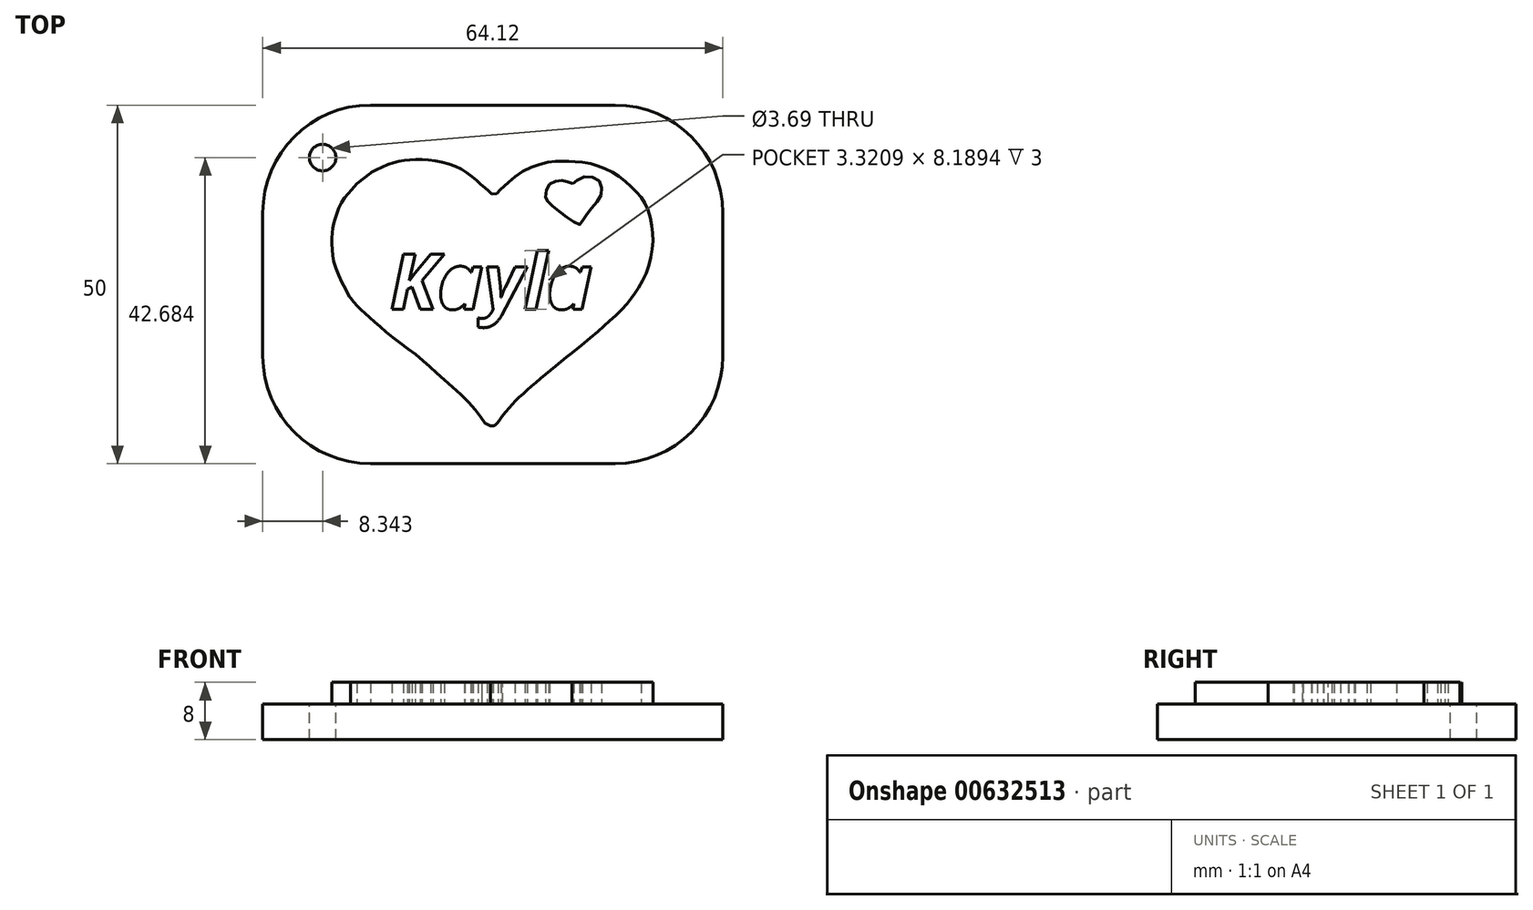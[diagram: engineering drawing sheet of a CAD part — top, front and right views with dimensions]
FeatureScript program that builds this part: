
annotation { "Feature Type Name" : "Feature", "Feature Type Description" : "" }
export const myFeature = defineFeature(function(context is Context, id is Id, definition is map)
    precondition{}
    {
        {
            var Q0;
            Q0=qCreatedBy(makeId("Top.planeOp"),FACE);
            var sketch = newSketch(context, id + "F0", { "sketchPlane" : qUnion([Q0])});
            skFitSpline(sketch, "E0", {"points": [v(-10.22, 16.07) * mm, v(-11.83, 17.48) * mm, v(-14.68, 19.6) * mm, v(-18.7, 20.74) * mm, v(-22.17, 20.77) * mm, v(-24.92, 20.07) * mm, v(-27.15, 18.98) * mm, v(-27.15, 18.96) * mm], "startDerivative": vector(-10.74, 9.94) * mm, "endDerivative": vector(0.77, -1.4) * mm});
            skFitSpline(sketch, "E1", {"points": [v(-29.04, 17.5) * mm, v(-27.15, 18.96) * mm], "startDerivative": vector(1.9, 1.45) * mm, "endDerivative": vector(1.9, 1.45) * mm});
            skFitSpline(sketch, "E2", {"points": [v(-29.04, 17.5) * mm, v(-29.87, 16.55) * mm, v(-31.22, 14.8) * mm, v(-32.12, 12.42) * mm, v(-32.46, 10.95) * mm, v(-32.51, 8.74) * mm, v(-32.07, 5.97) * mm, v(-30.44, 2.44) * mm, v(-29.97, 1.59) * mm, v(-29.92, 1.55) * mm], "startDerivative": vector(-7.96, -9.41) * mm, "endDerivative": vector(1.7, 0.61) * mm});
            skPoint(sketch, "E3.4.internal.orphan", {"position": v(-28.84, 0) * mm});
            skFitSpline(sketch, "E4", {"points": [v(-29.92, 1.55) * mm, v(-29.34, 0.8) * mm, v(-28.54, 0) * mm, v(-27.77, -0.74) * mm, v(-26.51, -1.83) * mm, v(-24.83, -3.28) * mm, v(-22.4, -5.19) * mm, v(-19.63, -7.33) * mm, v(-17.14, -9.63) * mm, v(-13.78, -12.64) * mm, v(-11.6, -15.33) * mm, v(-10.45, -16.28) * mm], "startDerivative": vector(9.33, -13.02) * mm, "endDerivative": vector(23.6, -0.7) * mm});
            skFitSpline(sketch, "E5", {"points": [v(-10.45, -16.28) * mm, v(-10.15, -16.28) * mm, v(-9.62, -16.03) * mm, v(-8.8, -14.99) * mm, v(-6.9, -12.79) * mm, v(-3.84, -10) * mm, v(0.92, -6.08) * mm], "startDerivative": vector(4.47, -0.42) * mm, "endDerivative": vector(17.48, 14.25) * mm});
            skFitSpline(sketch, "E6", {"points": [v(0.92, -6.08) * mm, v(4.47, -3.2) * mm, v(6.2, -1.62) * mm, v(7.96, 0) * mm, v(9.24, 1.54) * mm, v(10.05, 2.7) * mm, v(11.15, 4.8) * mm, v(11.9, 7.15) * mm, v(12.23, 9.6) * mm, v(12.05, 11.74) * mm, v(11.45, 13.98) * mm, v(10.59, 15.59) * mm], "startDerivative": vector(30.84, 24.32) * mm, "endDerivative": vector(-11.6, 18.83) * mm});
            skFitSpline(sketch, "E7", {"points": [v(10.59, 15.59) * mm, v(9.74, 16.54) * mm, v(8.74, 17.45) * mm, v(7.63, 18.4) * mm, v(6.4, 19.22) * mm, v(4.86, 19.85) * mm, v(3.79, 20.23) * mm, v(2.19, 20.5) * mm, v(1.1, 20.6) * mm, v(0, 20.6) * mm, v(-0.98, 20.6) * mm, v(-2.16, 20.53) * mm, v(-3.8, 20.13) * mm, v(-5.62, 19.4) * mm, v(-7.32, 18.23) * mm, v(-8.3, 17.37) * mm, v(-8.75, 16.96) * mm, v(-9.2, 16.5) * mm, v(-9.66, 16.08) * mm, v(-10.22, 16.07) * mm], "startDerivative": vector(-15.27, 18.1) * mm, "endDerivative": vector(-17.36, -0.4) * mm});
            skLineSegment(sketch, "E8", {"start": v(0.92, 17.65) * mm, "end": v(1.03, 17.5) * mm});
            skPoint(sketch, "E9.5.internal.orphan", {"position": v(0.72, 17.74) * mm});
            skPoint(sketch, "E10.6.internal.orphan", {"position": v(0, 13.29) * mm});
            skPoint(sketch, "E10.start.orphan", {"position": v(-1.58, 17.74) * mm});
            skPoint(sketch, "E11.1.internal.orphan", {"position": v(1.18, 17.5) * mm});
            skPoint(sketch, "E11.10.internal.orphan", {"position": v(5.07, 17.5) * mm});
            skFitSpline(sketch, "E12", {"points": [v(-1.92, 17.58) * mm, v(-2.49, 17.03) * mm, v(-2.78, 15.75) * mm, v(-2.68, 15.38) * mm, v(-2.28, 14.8) * mm, v(-1.48, 14.1) * mm, v(0.14, 12.9) * mm, v(1.34, 12.1) * mm, v(2.06, 11.83) * mm, v(2.48, 12.48) * mm, v(3.02, 13.29) * mm, v(3.77, 14.25) * mm, v(4.74, 15.39) * mm, v(5.07, 16.5) * mm, v(4.9, 17.64) * mm, v(3.99, 18.34) * mm, v(2.58, 18.46) * mm, v(1.43, 17.77) * mm, v(1.03, 17.5) * mm, v(0.47, 17.7) * mm, v(-0.21, 17.92) * mm, v(-1.05, 17.92) * mm, v(-1.92, 17.58) * mm]});
            skText(sketch, "E13", { "text": "Kayla", "fontName": "OpenSans-BoldItalic.ttf"});
            const initialGuessF0  = {"E13": [-0.02444, 0, 1, 0, 0.00776]};
            skSetInitialGuess(sketch, initialGuessF0);
            skSolve(sketch);
        }
        {
            var Q0;
            Q0=makeQuery(id+"F0.imprint","IMPRINT",FACE,{"disambiguationData":[TD([[makeQuery(id+"F0.imprint","IMPRINT",EDGE,{"derivedFrom":sQuery(id+"F0.wireOp",EDGE,"E0")}),1.0]])]});
            var Q1;
            Q1=makeQuery(id+"F0.imprint","IMPRINT",FACE,{"disambiguationData":[TD([[makeQuery(id+"F0.imprint","IMPRINT",EDGE,{"derivedFrom":sQuery(id+"F0.wireOp",EDGE,"f24f585c-4cd1-4648-b118-72204d16ea68.sketch_text.stroke-28")}),1.0]])]});
            var Q2;
            Q2=makeQuery(id+"F0.imprint","IMPRINT",FACE,{"disambiguationData":[TD([[makeQuery(id+"F0.imprint","IMPRINT",EDGE,{"derivedFrom":sQuery(id+"F0.wireOp",EDGE,"f24f585c-4cd1-4648-b118-72204d16ea68.sketch_text.stroke-74")}),1.0]])]});
            extrude(context, id + "F1", {"entities" : qUnion([Q0, Q1, Q2]), "depth" : 3 * mm, "offsetDistance" : 25 * mm});
        }
        {
            var Q0;
            Q0=makeQuery(id+"F1.opExtrude","CAP_FACE",FACE,{"disambiguationData":[OSD([sQuery(id+"F0.wireOp",EDGE,"E0"),sQuery(id+"F0.wireOp",EDGE,"E1"),sQuery(id+"F0.wireOp",EDGE,"E2"),sQuery(id+"F0.wireOp",EDGE,"E4"),sQuery(id+"F0.wireOp",EDGE,"E5"),sQuery(id+"F0.wireOp",EDGE,"E6"),sQuery(id+"F0.wireOp",EDGE,"E7"),sQuery(id+"F0.wireOp",EDGE,"f24f585c-4cd1-4648-b118-72204d16ea68.sketch_text.stroke-0"),sQuery(id+"F0.wireOp",EDGE,"f24f585c-4cd1-4648-b118-72204d16ea68.sketch_text.stroke-1"),sQuery(id+"F0.wireOp",EDGE,"f24f585c-4cd1-4648-b118-72204d16ea68.sketch_text.stroke-2"),sQuery(id+"F0.wireOp",EDGE,"f24f585c-4cd1-4648-b118-72204d16ea68.sketch_text.stroke-3"),sQuery(id+"F0.wireOp",EDGE,"f24f585c-4cd1-4648-b118-72204d16ea68.sketch_text.stroke-4"),sQuery(id+"F0.wireOp",EDGE,"f24f585c-4cd1-4648-b118-72204d16ea68.sketch_text.stroke-5"),sQuery(id+"F0.wireOp",EDGE,"f24f585c-4cd1-4648-b118-72204d16ea68.sketch_text.stroke-6"),sQuery(id+"F0.wireOp",EDGE,"f24f585c-4cd1-4648-b118-72204d16ea68.sketch_text.stroke-7"),sQuery(id+"F0.wireOp",EDGE,"f24f585c-4cd1-4648-b118-72204d16ea68.sketch_text.stroke-8"),sQuery(id+"F0.wireOp",EDGE,"f24f585c-4cd1-4648-b118-72204d16ea68.sketch_text.stroke-9"),sQuery(id+"F0.wireOp",EDGE,"f24f585c-4cd1-4648-b118-72204d16ea68.sketch_text.stroke-10"),sQuery(id+"F0.wireOp",EDGE,"f24f585c-4cd1-4648-b118-72204d16ea68.sketch_text.stroke-11"),sQuery(id+"F0.wireOp",EDGE,"f24f585c-4cd1-4648-b118-72204d16ea68.sketch_text.stroke-12"),sQuery(id+"F0.wireOp",EDGE,"f24f585c-4cd1-4648-b118-72204d16ea68.sketch_text.stroke-13"),sQuery(id+"F0.wireOp",EDGE,"f24f585c-4cd1-4648-b118-72204d16ea68.sketch_text.stroke-14"),sQuery(id+"F0.wireOp",EDGE,"f24f585c-4cd1-4648-b118-72204d16ea68.sketch_text.stroke-15"),sQuery(id+"F0.wireOp",EDGE,"f24f585c-4cd1-4648-b118-72204d16ea68.sketch_text.stroke-16"),sQuery(id+"F0.wireOp",EDGE,"f24f585c-4cd1-4648-b118-72204d16ea68.sketch_text.stroke-17"),sQuery(id+"F0.wireOp",EDGE,"f24f585c-4cd1-4648-b118-72204d16ea68.sketch_text.stroke-18"),sQuery(id+"F0.wireOp",EDGE,"f24f585c-4cd1-4648-b118-72204d16ea68.sketch_text.stroke-19"),sQuery(id+"F0.wireOp",EDGE,"f24f585c-4cd1-4648-b118-72204d16ea68.sketch_text.stroke-20"),sQuery(id+"F0.wireOp",EDGE,"f24f585c-4cd1-4648-b118-72204d16ea68.sketch_text.stroke-21"),sQuery(id+"F0.wireOp",EDGE,"f24f585c-4cd1-4648-b118-72204d16ea68.sketch_text.stroke-22"),sQuery(id+"F0.wireOp",EDGE,"f24f585c-4cd1-4648-b118-72204d16ea68.sketch_text.stroke-23"),sQuery(id+"F0.wireOp",EDGE,"f24f585c-4cd1-4648-b118-72204d16ea68.sketch_text.stroke-24"),sQuery(id+"F0.wireOp",EDGE,"f24f585c-4cd1-4648-b118-72204d16ea68.sketch_text.stroke-25"),sQuery(id+"F0.wireOp",EDGE,"f24f585c-4cd1-4648-b118-72204d16ea68.sketch_text.stroke-26"),sQuery(id+"F0.wireOp",EDGE,"f24f585c-4cd1-4648-b118-72204d16ea68.sketch_text.stroke-27"),sQuery(id+"F0.wireOp",EDGE,"f24f585c-4cd1-4648-b118-72204d16ea68.sketch_text.stroke-38"),sQuery(id+"F0.wireOp",EDGE,"f24f585c-4cd1-4648-b118-72204d16ea68.sketch_text.stroke-39"),sQuery(id+"F0.wireOp",EDGE,"f24f585c-4cd1-4648-b118-72204d16ea68.sketch_text.stroke-40"),sQuery(id+"F0.wireOp",EDGE,"f24f585c-4cd1-4648-b118-72204d16ea68.sketch_text.stroke-41"),sQuery(id+"F0.wireOp",EDGE,"f24f585c-4cd1-4648-b118-72204d16ea68.sketch_text.stroke-42"),sQuery(id+"F0.wireOp",EDGE,"f24f585c-4cd1-4648-b118-72204d16ea68.sketch_text.stroke-43"),sQuery(id+"F0.wireOp",EDGE,"f24f585c-4cd1-4648-b118-72204d16ea68.sketch_text.stroke-44"),sQuery(id+"F0.wireOp",EDGE,"f24f585c-4cd1-4648-b118-72204d16ea68.sketch_text.stroke-45"),sQuery(id+"F0.wireOp",EDGE,"f24f585c-4cd1-4648-b118-72204d16ea68.sketch_text.stroke-46"),sQuery(id+"F0.wireOp",EDGE,"f24f585c-4cd1-4648-b118-72204d16ea68.sketch_text.stroke-47"),sQuery(id+"F0.wireOp",EDGE,"f24f585c-4cd1-4648-b118-72204d16ea68.sketch_text.stroke-48"),sQuery(id+"F0.wireOp",EDGE,"f24f585c-4cd1-4648-b118-72204d16ea68.sketch_text.stroke-49"),sQuery(id+"F0.wireOp",EDGE,"f24f585c-4cd1-4648-b118-72204d16ea68.sketch_text.stroke-50"),sQuery(id+"F0.wireOp",EDGE,"f24f585c-4cd1-4648-b118-72204d16ea68.sketch_text.stroke-51"),sQuery(id+"F0.wireOp",EDGE,"f24f585c-4cd1-4648-b118-72204d16ea68.sketch_text.stroke-52"),sQuery(id+"F0.wireOp",EDGE,"f24f585c-4cd1-4648-b118-72204d16ea68.sketch_text.stroke-53"),sQuery(id+"F0.wireOp",EDGE,"f24f585c-4cd1-4648-b118-72204d16ea68.sketch_text.stroke-54"),sQuery(id+"F0.wireOp",EDGE,"f24f585c-4cd1-4648-b118-72204d16ea68.sketch_text.stroke-55"),sQuery(id+"F0.wireOp",EDGE,"f24f585c-4cd1-4648-b118-72204d16ea68.sketch_text.stroke-56"),sQuery(id+"F0.wireOp",EDGE,"f24f585c-4cd1-4648-b118-72204d16ea68.sketch_text.stroke-57"),sQuery(id+"F0.wireOp",EDGE,"f24f585c-4cd1-4648-b118-72204d16ea68.sketch_text.stroke-58"),sQuery(id+"F0.wireOp",EDGE,"f24f585c-4cd1-4648-b118-72204d16ea68.sketch_text.stroke-59"),sQuery(id+"F0.wireOp",EDGE,"f24f585c-4cd1-4648-b118-72204d16ea68.sketch_text.stroke-60"),sQuery(id+"F0.wireOp",EDGE,"f24f585c-4cd1-4648-b118-72204d16ea68.sketch_text.stroke-61"),sQuery(id+"F0.wireOp",EDGE,"f24f585c-4cd1-4648-b118-72204d16ea68.sketch_text.stroke-62"),sQuery(id+"F0.wireOp",EDGE,"f24f585c-4cd1-4648-b118-72204d16ea68.sketch_text.stroke-63"),sQuery(id+"F0.wireOp",EDGE,"f24f585c-4cd1-4648-b118-72204d16ea68.sketch_text.stroke-64"),sQuery(id+"F0.wireOp",EDGE,"f24f585c-4cd1-4648-b118-72204d16ea68.sketch_text.stroke-65"),sQuery(id+"F0.wireOp",EDGE,"f24f585c-4cd1-4648-b118-72204d16ea68.sketch_text.stroke-66"),sQuery(id+"F0.wireOp",EDGE,"f24f585c-4cd1-4648-b118-72204d16ea68.sketch_text.stroke-67"),sQuery(id+"F0.wireOp",EDGE,"f24f585c-4cd1-4648-b118-72204d16ea68.sketch_text.stroke-68"),sQuery(id+"F0.wireOp",EDGE,"f24f585c-4cd1-4648-b118-72204d16ea68.sketch_text.stroke-69"),sQuery(id+"F0.wireOp",EDGE,"f24f585c-4cd1-4648-b118-72204d16ea68.sketch_text.stroke-70"),sQuery(id+"F0.wireOp",EDGE,"f24f585c-4cd1-4648-b118-72204d16ea68.sketch_text.stroke-71"),sQuery(id+"F0.wireOp",EDGE,"f24f585c-4cd1-4648-b118-72204d16ea68.sketch_text.stroke-72"),sQuery(id+"F0.wireOp",EDGE,"f24f585c-4cd1-4648-b118-72204d16ea68.sketch_text.stroke-73"),sQuery(id+"F0.wireOp",EDGE,"E12")])],"isStart":true});
            var sketch = newSketch(context, id + "F2", { "sketchPlane" : qUnion([Q0])});
            skLineSegment(sketch, "E14.bottom", {"start": v(21.96, 21.55) * mm, "end": v(-42.16, 21.55) * mm});
            skLineSegment(sketch, "E14.top", {"start": v(21.96, -28.45) * mm, "end": v(-42.16, -28.45) * mm});
            skLineSegment(sketch, "E14.left", {"start": v(21.96, 21.55) * mm, "end": v(21.96, -28.45) * mm});
            skLineSegment(sketch, "E14.right", {"start": v(-42.16, 21.55) * mm, "end": v(-42.16, -28.45) * mm});
            skCircle(sketch, "E15", {"center": v(-33.82, -21.13) * mm, "radius": 1.85 * mm});
            skSolve(sketch);
        }
        {
            var Q0;
            Q0 = qSketchRegion(id + "F2", true);
            extrude(context, id + "F3", {"entities" : qUnion([Q0]), "operationType" : NewBodyOperationType.ADD, "depth" : 5 * mm, "offsetDistance" : 25 * mm});
        }
        {
            var Q0;
            Q0=makeQuery(id+"F3.opExtrude","SWEPT_EDGE",EDGE,{"disambiguationData":[OSD([sQuery(id+"F2.wireOp",EDGE,"E14.top"),sQuery(id+"F2.wireOp",EDGE,"E14.right")])]});
            var Q1;
            Q1=makeQuery(id+"F3.opExtrude","SWEPT_EDGE",EDGE,{"disambiguationData":[OSD([sQuery(id+"F2.wireOp",EDGE,"E14.bottom"),sQuery(id+"F2.wireOp",EDGE,"E14.right")])]});
            var Q2;
            Q2=makeQuery(id+"F3.opExtrude","SWEPT_EDGE",EDGE,{"disambiguationData":[OSD([sQuery(id+"F2.wireOp",EDGE,"E14.top"),sQuery(id+"F2.wireOp",EDGE,"E14.left")])]});
            var Q3;
            Q3=makeQuery(id+"F3.opExtrude","SWEPT_EDGE",EDGE,{"disambiguationData":[OSD([sQuery(id+"F2.wireOp",EDGE,"E14.bottom"),sQuery(id+"F2.wireOp",EDGE,"E14.left")])]});
            fillet(context, id + "F4", {"entities" : qUnion([Q0, Q1, Q2, Q3]), "radius" : 15 * mm, "tangentPropagation" : true, "allowEdgeOverflow" : false});
        }
    });
